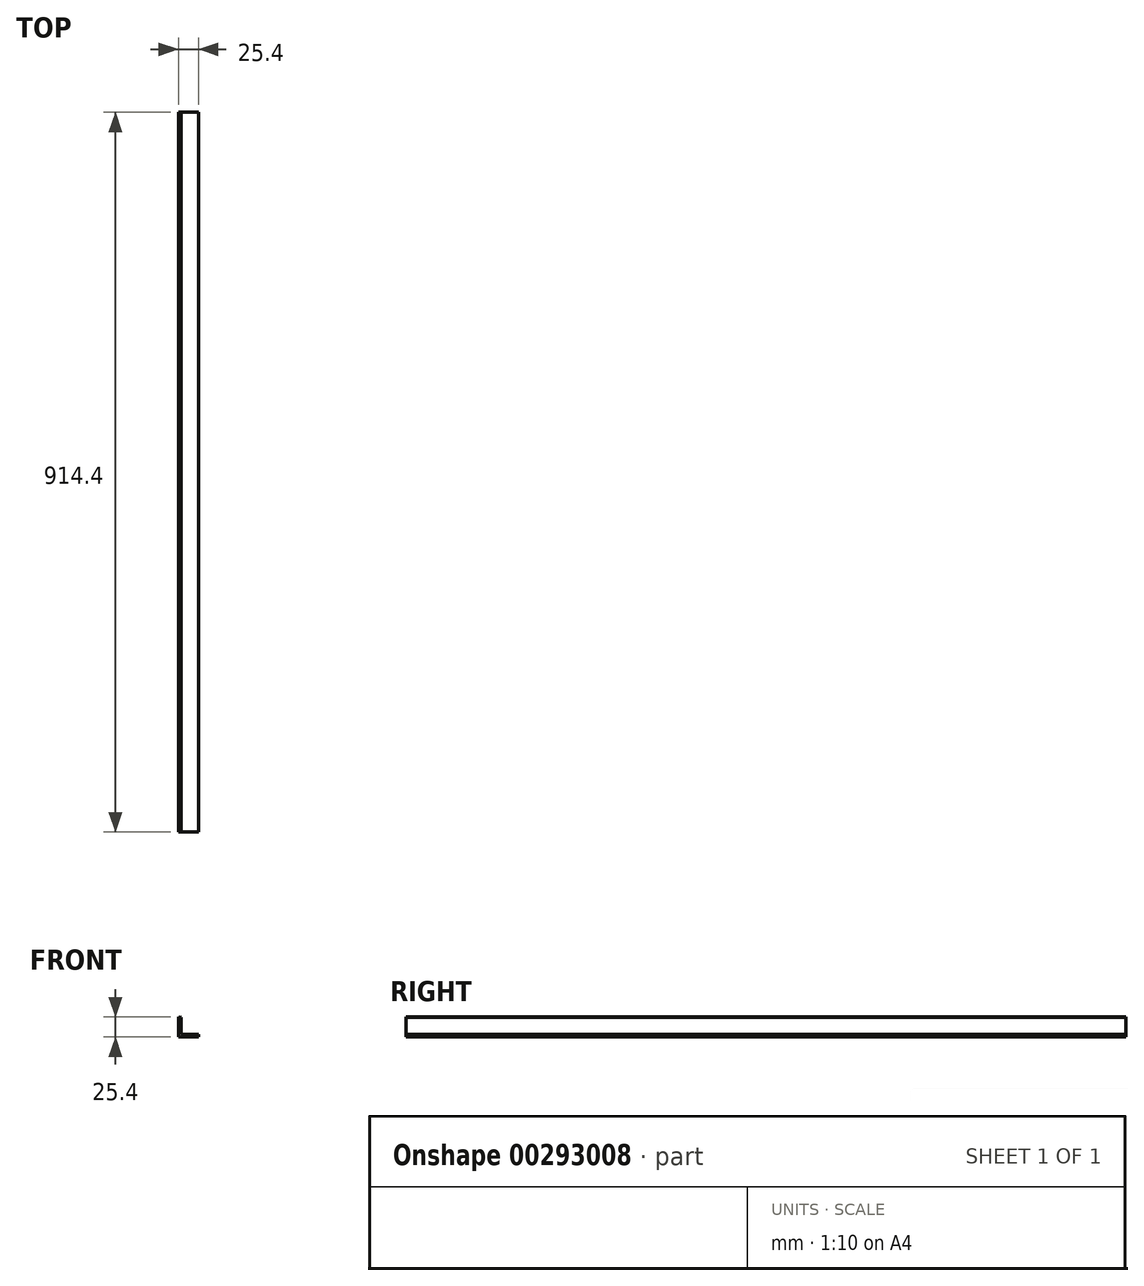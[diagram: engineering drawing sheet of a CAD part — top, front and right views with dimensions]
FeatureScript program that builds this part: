
annotation { "Feature Type Name" : "Feature", "Feature Type Description" : "" }
export const myFeature = defineFeature(function(context is Context, id is Id, definition is map)
    precondition{}
    {
        {
            var Q0;
            Q0=qCreatedBy(makeId("Front.planeOp"),FACE);
            var sketch = newSketch(context, id + "F0", { "sketchPlane" : qUnion([Q0])});
            skLineSegment(sketch, "E0", {"start": v(0, 25.4) * mm, "end": v(0, 0) * mm});
            skLineSegment(sketch, "E1", {"start": v(0, 0) * mm, "end": v(25.4, 0) * mm});
            skLineSegment(sketch, "E2", {"start": v(25.4, 0) * mm, "end": v(25.4, 3.18) * mm});
            skLineSegment(sketch, "E3", {"start": v(25.4, 3.18) * mm, "end": v(3.17, 3.17) * mm});
            skLineSegment(sketch, "E4", {"start": v(3.17, 3.18) * mm, "end": v(3.17, 25.3) * mm});
            skLineSegment(sketch, "E5", {"start": v(3.17, 25.3) * mm, "end": v(0, 25.4) * mm});
            skSolve(sketch);
        }
        {
            var Q0;
            Q0=makeQuery(id+"F0.imprint","IMPRINT",FACE,{"disambiguationData":[TD([[makeQuery(id+"F0.imprint","IMPRINT",EDGE,{"derivedFrom":sQuery(id+"F0.wireOp",EDGE,"E0")}),1.0]])]});
            extrude(context, id + "F1", {"entities" : qUnion([Q0]), "depth" : 914.4 * mm});
        }
    });
